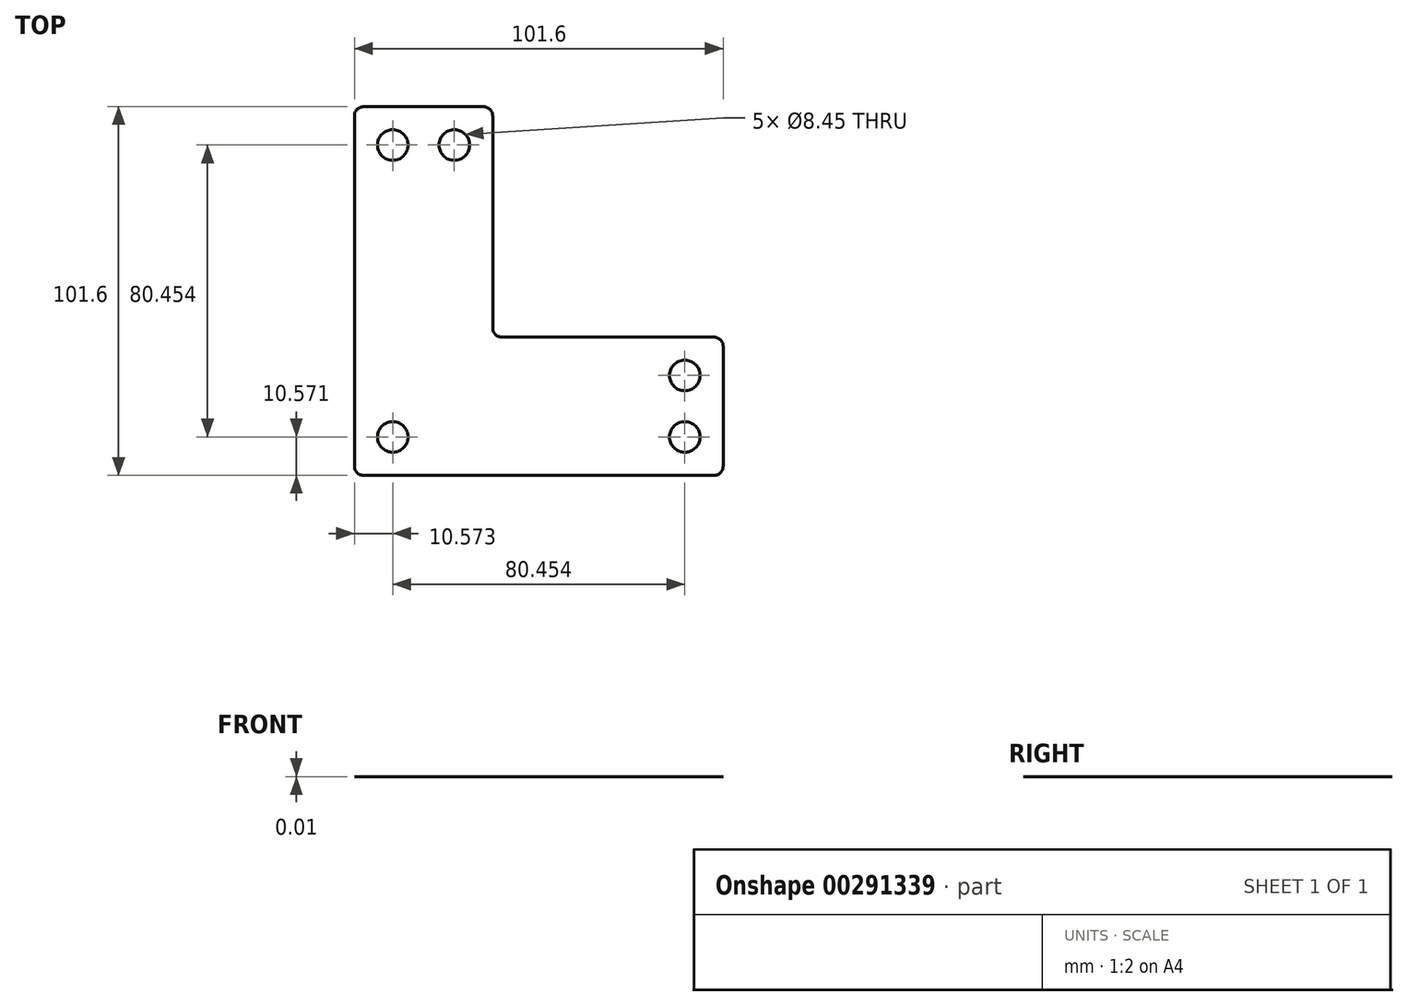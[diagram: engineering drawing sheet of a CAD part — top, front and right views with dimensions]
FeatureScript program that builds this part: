
annotation { "Feature Type Name" : "Feature", "Feature Type Description" : "" }
export const myFeature = defineFeature(function(context is Context, id is Id, definition is map)
    precondition{}
    {
        {
            var Q0;
            Q0=qCreatedBy(makeId("Top.planeOp"),FACE);
            var sketch = newSketch(context, id + "F0", { "sketchPlane" : qUnion([Q0])});
            skLineSegment(sketch, "E0", {"start": v(-38.1, 78.94) * mm, "end": v(-38.1, -22.66) * mm});
            skLineSegment(sketch, "E1", {"start": v(-38.1, -22.66) * mm, "end": v(63.5, -22.66) * mm});
            skLineSegment(sketch, "E2", {"start": v(63.5, -22.66) * mm, "end": v(63.5, 15.44) * mm});
            skLineSegment(sketch, "E3", {"start": v(63.5, 15.44) * mm, "end": v(0, 15.44) * mm});
            skLineSegment(sketch, "E4", {"start": v(0, 15.44) * mm, "end": v(0, 78.94) * mm});
            skLineSegment(sketch, "E5", {"start": v(0, 78.94) * mm, "end": v(-38.1, 78.94) * mm});
            skSolve(sketch);
        }
        {
            var Q0;
            Q0 = qSketchRegion(id + "F0", true);
            extrude(context, id + "F1", {"entities" : qUnion([Q0]), "depth" : 1 / 101.6 * mm});
        }
        {
            var Q0;
            Q0=makeQuery(id+"F1.opExtrude","CAP_FACE",FACE,{"disambiguationData":[OSD([sQuery(id+"F0.wireOp",EDGE,"E0"),sQuery(id+"F0.wireOp",EDGE,"E1"),sQuery(id+"F0.wireOp",EDGE,"E2"),sQuery(id+"F0.wireOp",EDGE,"E3"),sQuery(id+"F0.wireOp",EDGE,"E4"),sQuery(id+"F0.wireOp",EDGE,"E5")])],"isStart":false});
            var sketch = newSketch(context, id + "F2", { "sketchPlane" : qUnion([Q0])});
            skCircle(sketch, "E6", {"center": v(-27.53, 68.37) * mm, "radius": 4.22 * mm});
            skCircle(sketch, "E7", {"center": v(-10.57, 68.37) * mm, "radius": 4.22 * mm});
            skCircle(sketch, "E8", {"center": v(52.93, 4.87) * mm, "radius": 4.22 * mm});
            skCircle(sketch, "E9", {"center": v(52.93, -12.09) * mm, "radius": 4.22 * mm});
            skCircle(sketch, "E10", {"center": v(-27.53, -12.09) * mm, "radius": 4.22 * mm});
            skSolve(sketch);
        }
        {
            var Q0;
            Q0 = qSketchRegion(id + "F2", true);
            extrude(context, id + "F3", {"entities" : qUnion([Q0]), "operationType" : NewBodyOperationType.REMOVE, "endBound" : BoundingType.THROUGH_ALL, "oppositeDirection" : true, "depth" : 25.4 * mm});
        }
        {
            var Q0;
            Q0=makeQuery(id+"F1.opExtrude","SWEPT_EDGE",EDGE,{"disambiguationData":[OSD([sQuery(id+"F0.wireOp",EDGE,"E0"),sQuery(id+"F0.wireOp",EDGE,"E1")])]});
            var Q1;
            Q1=makeQuery(id+"F1.opExtrude","SWEPT_EDGE",EDGE,{"disambiguationData":[OSD([sQuery(id+"F0.wireOp",EDGE,"E1"),sQuery(id+"F0.wireOp",EDGE,"E2")])]});
            var Q2;
            Q2=makeQuery(id+"F1.opExtrude","SWEPT_EDGE",EDGE,{"disambiguationData":[OSD([sQuery(id+"F0.wireOp",EDGE,"E2"),sQuery(id+"F0.wireOp",EDGE,"E3")])]});
            var Q3;
            Q3=makeQuery(id+"F1.opExtrude","SWEPT_EDGE",EDGE,{"disambiguationData":[OSD([sQuery(id+"F0.wireOp",EDGE,"E3"),sQuery(id+"F0.wireOp",EDGE,"E4")])]});
            var Q4;
            Q4=makeQuery(id+"F1.opExtrude","SWEPT_EDGE",EDGE,{"disambiguationData":[OSD([sQuery(id+"F0.wireOp",EDGE,"E4"),sQuery(id+"F0.wireOp",EDGE,"E5")])]});
            var Q5;
            Q5=makeQuery(id+"F1.opExtrude","SWEPT_EDGE",EDGE,{"disambiguationData":[OSD([sQuery(id+"F0.wireOp",EDGE,"E0"),sQuery(id+"F0.wireOp",EDGE,"E5")])]});
            fillet(context, id + "F4", {"entities" : qUnion([Q0, Q1, Q2, Q3, Q4, Q5]), "radius" : 2.54 * mm, "tangentPropagation" : true, "allowEdgeOverflow" : false});
        }
    });
